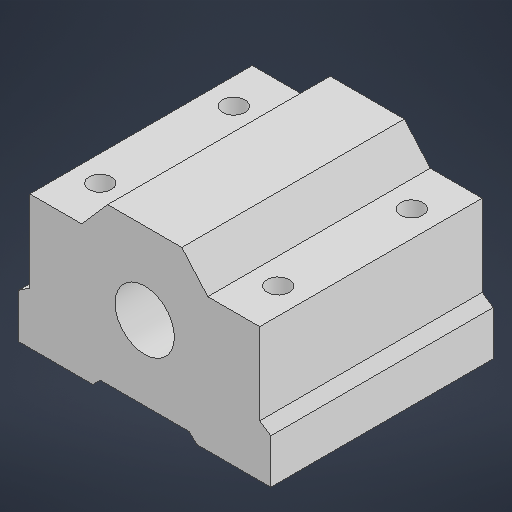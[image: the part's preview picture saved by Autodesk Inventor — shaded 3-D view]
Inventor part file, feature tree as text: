
AUTODESK INVENTOR PART (.ipt)
format: ipt  version: 2025.1 (Build 291241000, 241)  size: 190,464 bytes
history: native  units: mm
features: extrude x2, sketch x2
ambient origin geometry x8: Origin, YZ Plane, XZ Plane, XY Plane, X Axis, Y Axis, Z Axis, Center Point
bodies: Solid1 (feature_tree)
feature tree (4):
  extrude  "Extrusion1"  Depth=15.5mm
  extrude  "Extrusion2"  Depth=17.0mm
  sketch  "Sketch1"  dims[d0=8.0mm d1=15.5mm]
  sketch  "Sketch2"  dims[d2=11.0mm d3=17.0mm d4=6.0mm d5=18.0mm d6=22.0mm d7=5.0mm d8=7.0mm d9=30.0mm d10=0.0mm d11=3.0mm d12=24.0mm d13=18.0mm d14=3.0mm d15=3.0mm d16=3.0mm d17=0.0mm d18=0.0mm d19=10.0mm d20=1.0mm d21=6.0mm]
